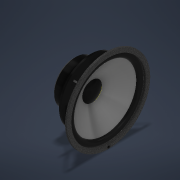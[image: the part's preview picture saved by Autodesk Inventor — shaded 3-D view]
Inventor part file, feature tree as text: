
AUTODESK INVENTOR PART (.ipt)
format: ipt  version: 2022 (Build 260153070, 153G)  size: 670,720 bytes
history: native  units: mm
features: other x11, sketch x6, pattern_circular x2, revolve x1, hole x1, extrude x1
ambient origin geometry x8: Origin, YZ Plane, XZ Plane, XY Plane, X Axis, Y Axis, Z Axis, Center Point
bodies: Body1 (feature_tree)
feature tree (22):
  other  "Твердое тело1"
  revolve  "Вращение1"
  sketch  "Эскиз2"
  sketch  "Эскиз3"
  pattern_circular  "Круговой массив1"  [2 undecoded]
  hole  "Отверстие2"  [1 undecoded]
  sketch  "Эскиз5"
  extrude  "Выдавливание1"  Depth=6.0mm
  pattern_circular  "Круговой массив2"  Angle=360.0deg  [1 undecoded]
  other  "Непосредственное редактирование1"
  other  "Непосредственное редактирование2"
  other  "Непосредственное редактирование3"
  other  "Непосредственное редактирование4"
  other  "Непосредственное редактирование5"
  sketch  "Эскиз1"
  sketch  "Эскиз4"
  sketch  "Эскиз6"
  other  "Масштаб1"
  other  "Масштаб2"
  other  "Масштаб3"
  other  "Масштаб4"
  other  "Масштаб5"
note: 4 required parameter values undecoded (feature->parameter linkage not recoverable at this tier; creation-order binding heuristic only, values carry confidence <= 0.55)
